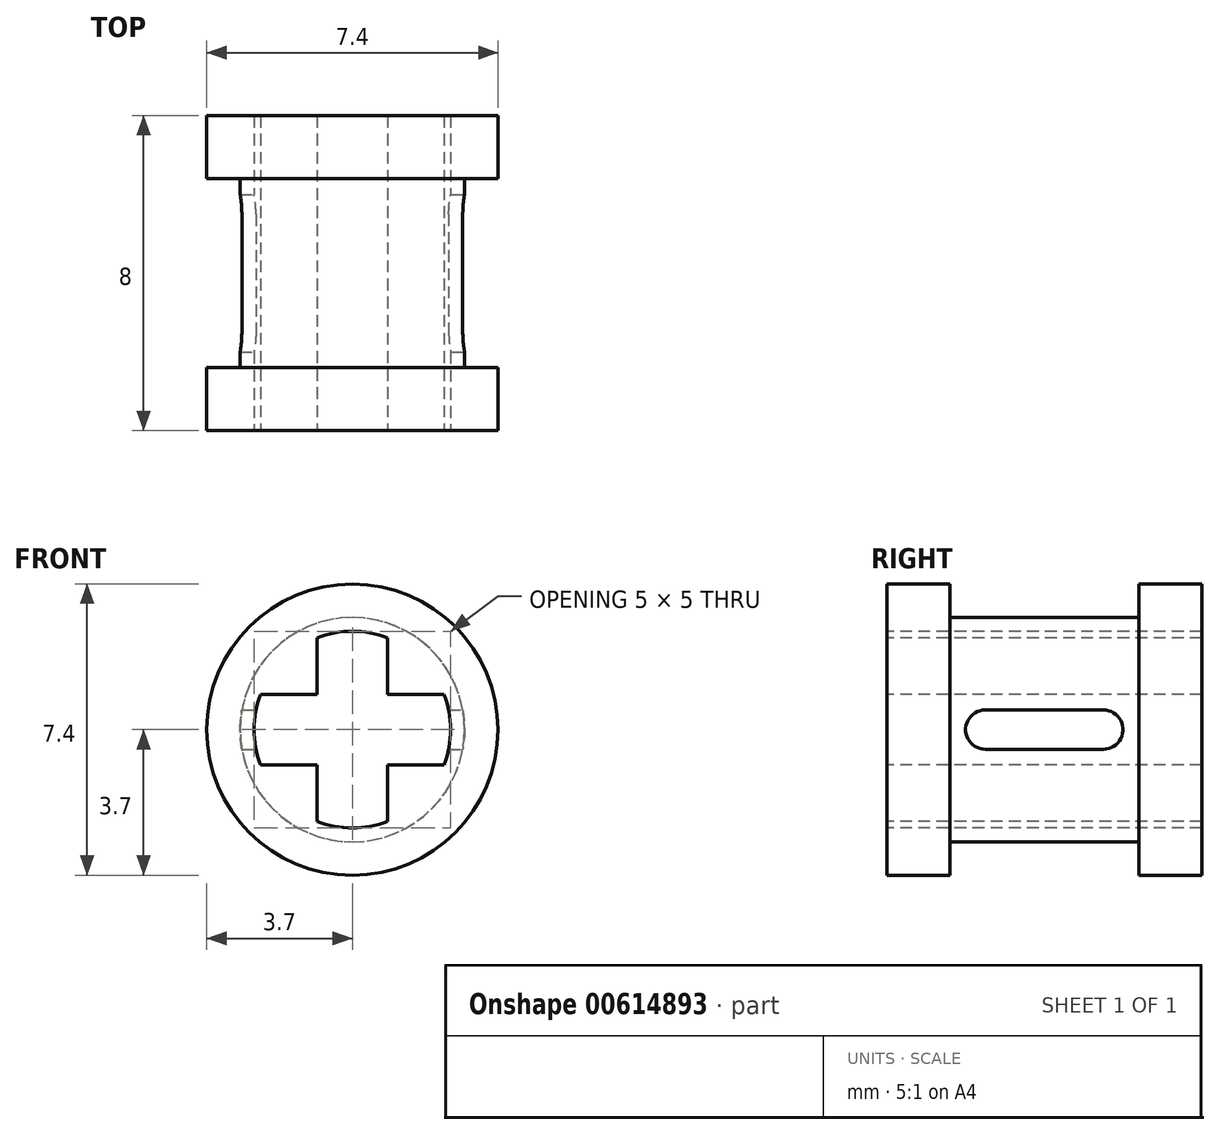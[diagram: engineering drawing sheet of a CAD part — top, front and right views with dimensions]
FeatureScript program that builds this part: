
annotation { "Feature Type Name" : "Feature", "Feature Type Description" : "" }
export const myFeature = defineFeature(function(context is Context, id is Id, definition is map)
    precondition{}
    {
        {
            var Q0;
            Q0=qCreatedBy(makeId("Front.planeOp"),FACE);
            var sketch = newSketch(context, id + "F0", { "sketchPlane" : qUnion([Q0])});
            skCircle(sketch, "E0", {"center": v(0, 0) * mm, "radius": 2.85 * mm});
            skSolve(sketch);
        }
        {
            var Q0;
            Q0=makeQuery(id+"F0.imprint","IMPRINT",FACE,{"disambiguationData":[TD([[makeQuery(id+"F0.imprint","IMPRINT",EDGE,{"derivedFrom":sQuery(id+"F0.wireOp",EDGE,"E0")}),1.0]])]});
            extrude(context, id + "F1", {"entities" : qUnion([Q0]), "endBound" : BoundingType.SYMMETRIC, "depth" : 8 * mm, "offsetDistance" : 25 * mm});
        }
        {
            var Q0;
            Q0=makeQuery(id+"F1.opExtrude","CAP_FACE",FACE,{"disambiguationData":[OSD([sQuery(id+"F0.wireOp",EDGE,"E0")])],"isStart":false});
            var sketch = newSketch(context, id + "F2", { "sketchPlane" : qUnion([Q0])});
            skCircle(sketch, "E1", {"center": v(0, 0) * mm, "radius": 3.7 * mm});
            skSolve(sketch);
        }
        {
            var Q0;
            Q0=makeQuery(id+"F2.imprint","IMPRINT",FACE,{"disambiguationData":[TD([[makeQuery(id+"F2.imprint","IMPRINT",EDGE,{"derivedFrom":sQuery(id+"F2.wireOp",EDGE,"E1")}),1.0]])]});
            extrude(context, id + "F3", {"entities" : qUnion([Q0]), "operationType" : NewBodyOperationType.ADD, "oppositeDirection" : true, "depth" : 1.6 * mm, "offsetDistance" : 25 * mm});
        }
        {
            var Q0;
            Q0=makeQuery(id+"F1.opExtrude","CAP_FACE",FACE,{"disambiguationData":[OSD([sQuery(id+"F0.wireOp",EDGE,"E0")])],"isStart":true});
            var sketch = newSketch(context, id + "F4", { "sketchPlane" : qUnion([Q0])});
            skCircle(sketch, "E2", {"center": v(0, 0) * mm, "radius": 3.7 * mm});
            skSolve(sketch);
        }
        {
            var Q0;
            Q0=makeQuery(id+"F4.imprint","IMPRINT",FACE,{"disambiguationData":[TD([[makeQuery(id+"F4.imprint","IMPRINT",EDGE,{"derivedFrom":sQuery(id+"F4.wireOp",EDGE,"E2")}),1.0]])]});
            extrude(context, id + "F5", {"entities" : qUnion([Q0]), "operationType" : NewBodyOperationType.ADD, "oppositeDirection" : true, "depth" : 1.6 * mm, "offsetDistance" : 25 * mm});
        }
        {
            var Q0;
            {var subQ0=sQuery(id+"F0.wireOp",EDGE,"E0");Q0=makeQuery(id+"F3.boolean.opBoolean","MERGE",FACE,{"derivedFrom":[makeQuery(id+"F1.opExtrude","CAP_FACE",FACE,{"disambiguationData":[OSD([subQ0])],"isStart":false}),makeQuery(id+"F3.opExtrude","CAP_FACE",FACE,{"disambiguationData":[OSD([subQ0,sQuery(id+"F2.wireOp",EDGE,"E1")])],"isStart":true})]});}
            var sketch = newSketch(context, id + "F6", { "sketchPlane" : qUnion([Q0])});
            skCircle(sketch, "E3", {"center": v(0, 0) * mm, "radius": 2.5 * mm});
            skLineSegment(sketch, "E4", {"start": v(0, 0) * mm, "end": v(0, 0.9) * mm});
            skLineSegment(sketch, "E5", {"start": v(0, 0) * mm, "end": v(0, -0.9) * mm});
            skLineSegment(sketch, "E6", {"start": v(0.9, 0.9) * mm, "end": v(2.33, 0.9) * mm});
            skLineSegment(sketch, "E7", {"start": v(0.9, 0.9) * mm, "end": v(0.9, 2.33) * mm});
            skLineSegment(sketch, "E8", {"start": v(0.9, -0.9) * mm, "end": v(2.33, -0.9) * mm});
            skLineSegment(sketch, "E9", {"start": v(-0.9, -0.9) * mm, "end": v(-2.33, -0.9) * mm});
            skLineSegment(sketch, "E10", {"start": v(-0.9, -0.9) * mm, "end": v(-0.9, -2.33) * mm});
            skLineSegment(sketch, "E11", {"start": v(-0.9, 0.9) * mm, "end": v(-0.9, 2.33) * mm});
            skLineSegment(sketch, "E12", {"start": v(-0.9, 0.9) * mm, "end": v(-2.33, 0.9) * mm});
            skLineSegment(sketch, "E13", {"start": v(0.9, -0.9) * mm, "end": v(0.9, -2.33) * mm});
            skSolve(sketch);
        }
        {
            var Q0;
            {var subQ4=sQuery(id+"F6.wireOp",EDGE,"E6");Q0=makeQuery(id+"F6.imprint","IMPRINT",FACE,{"disambiguationData":[TD([[makeQuery(id+"F6.imprint","IMPRINT",EDGE,{"derivedFrom":subQ4}),-1.0]])]});}
            extrude(context, id + "F7", {"entities" : qUnion([Q0]), "operationType" : NewBodyOperationType.REMOVE, "endBound" : BoundingType.THROUGH_ALL, "oppositeDirection" : true, "depth" : 25 * mm, "offsetDistance" : 25 * mm});
        }
        {
            var Q0;
            Q0=qCreatedBy(makeId("Right.planeOp"),FACE);
            var sketch = newSketch(context, id + "F8", { "sketchPlane" : qUnion([Q0])});
            skLineSegment(sketch, "E14", {"start": v(0, 0) * mm, "end": v(-2, 0) * mm});
            skLineSegment(sketch, "E15", {"start": v(-2, 0) * mm, "end": v(2, 0) * mm});
            skLineSegment(sketch, "E16", {"start": v(0, 0) * mm, "end": v(0, 0.5) * mm});
            skLineSegment(sketch, "E17", {"start": v(0, 0.5) * mm, "end": v(-1.5, 0.5) * mm});
            skLineSegment(sketch, "E18", {"start": v(-1.5, 0.5) * mm, "end": v(1.5, 0.5) * mm});
            skLineSegment(sketch, "E19", {"start": v(1.5, -0.5) * mm, "end": v(-1.5, -0.5) * mm});
            skLineSegment(sketch, "E20", {"start": v(0, 0) * mm, "end": v(-1.5, 0) * mm});
            skArc(sketch, "E21", {"start": v(-1.5, 0.5) * mm, "mid": v(-2, 0) * mm, "end": v(-1.5, -0.5) * mm});
            skLineSegment(sketch, "E22", {"start": v(0, 0) * mm, "end": v(1.5, 0) * mm});
            skArc(sketch, "E23", {"start": v(1.5, -0.5) * mm, "mid": v(2, 0) * mm, "end": v(1.5, 0.5) * mm});
            skPoint(sketch, "E24.orphan", {"position": v(2, 0.5) * mm});
            skPoint(sketch, "E25.orphan", {"position": v(-2, 0.5) * mm});
            skPoint(sketch, "E26.orphan", {"position": v(-2, -0.5) * mm});
            skSolve(sketch);
        }
        {
            var Q0;
            Q0 = qSketchRegion(id + "F8", true);
            extrude(context, id + "F9", {"entities" : qUnion([Q0]), "operationType" : NewBodyOperationType.REMOVE, "endBound" : BoundingType.SYMMETRIC, "oppositeDirection" : true, "depth" : 25 * mm, "offsetDistance" : 25 * mm});
        }
    });
